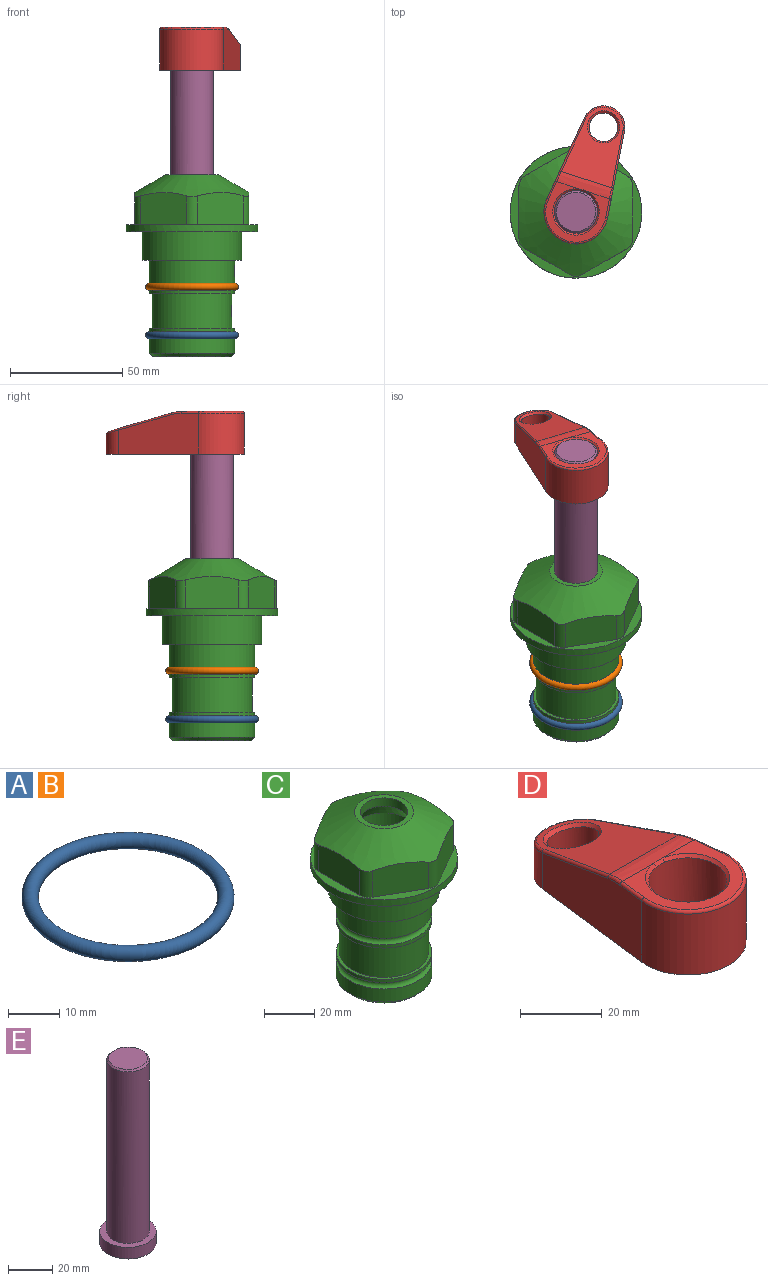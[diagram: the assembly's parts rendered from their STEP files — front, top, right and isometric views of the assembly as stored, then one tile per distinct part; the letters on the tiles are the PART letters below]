
ASSEMBLY  parts=5 mates=4
PART A: 1 faces, bbox 44.7x44.7x3.2 mm
  f0: torus R=19.05mm, axis (0,0,1), area 1193.9mm2
PART B: same geometry as A
PART C: 36 faces, bbox 58.7x58.7x81 mm
  f0: cylinder r=17.78mm len=35.56mm, axis (0,0,1), area 1670.8mm2, adj f23,f24,f31
  f1: cylinder r=19.05mm len=38.1mm, axis (0,0,1), area 1191.9mm2, adj f26,f27,f30
  f2: plane 58.66x58.66mm, normal (0,0,-1), area 1150.6mm2, adj f3,f28
  f3: cylinder r=29.33mm len=58.66mm, axis (0,0,-1), area 585.1mm2, adj f2,f4
  f4: plane 58.66x58.66mm, normal (0,0,1), area 475.9mm2, adj f3,f5,f6,f7,f8,f9,f10,f11
  f5: plane 20.32x14.34mm, normal (-0.5,0.87,0), area 324.4mm2, adj f4,f15,f16,f17
  f6: plane 20.32x14.34mm, normal (0.5,0.87,0), area 324.4mm2, adj f4,f14,f15,f17
  f7: plane 23.48x14.34mm, normal (1,0,0), area 324.4mm2, adj f4,f13,f14,f17
  f8: plane 20.32x14.34mm, normal (0.5,-0.87,0), area 324.4mm2, adj f4,f12,f13,f17
  f9: plane 20.32x14.34mm, normal (-0.5,-0.87,0), area 324.4mm2, adj f4,f11,f12,f17
  f10: plane 23.48x14.34mm, normal (-1,0,0), area 324.4mm2, adj f4,f11,f16,f17
  f11: cylinder r=5.08mm len=12.85mm, axis (0,0,-1), area 67.2mm2, adj f4,f9,f10,f17
  f12: cylinder r=5.08mm len=12.85mm, axis (0,0,-1), area 67.2mm2, adj f4,f8,f9,f17
  f13: cylinder r=5.08mm len=12.85mm, axis (0,0,-1), area 67.2mm2, adj f4,f7,f8,f17
  f14: cylinder r=5.08mm len=12.85mm, axis (0,0,-1), area 67.2mm2, adj f4,f6,f7,f17
  f15: cylinder r=5.08mm len=12.85mm, axis (0,0,-1), area 67.2mm2, adj f4,f5,f6,f17
  f16: cylinder r=5.08mm len=12.85mm, axis (0,0,-1), area 67.2mm2, adj f4,f5,f10,f17
  f17: cone r=11.73mm half-angle=60deg, axis (0,0,-1), area 2071.8mm2, adj f5,f6,f7,f8,f9,f10,f11,f12
  f18: plane 23.46x23.46mm, normal (0,0,1), area 147.4mm2, adj f17,f35
  f19: plane 34.93x34.93mm, normal (0,0,-1), area 958mm2, adj f29
  f20: cylinder r=19.05mm len=38.1mm, axis (0,0,1), area 760.1mm2, adj f21,f29
  f21: torus R=19.05mm, axis (0,0,1), area 565.3mm2, adj f20,f22
  f22: cylinder r=19.05mm len=38.1mm, axis (0,0,1), area 190mm2, adj f21,f23
  f23: plane 38.1x38.1mm, normal (0,0,1), area 146.9mm2, adj f0,f22
  f24: plane 38.1x38.1mm, normal (0,0,-1), area 146.9mm2, adj f0,f25
  f25: cylinder r=19.05mm len=38.1mm, axis (0,0,1), area 190mm2, adj f24,f26
  f26: torus R=19.05mm, axis (0,0,1), area 565.3mm2, adj f1,f25
  f27: plane 44.45x44.45mm, normal (0,0,-1), area 411.7mm2, adj f1,f28
  f28: cylinder r=22.23mm len=44.45mm, axis (0,0,1), area 1773.5mm2, adj f2,f27
  f29: cone r=19.05mm half-angle=45deg, axis (0,0,1), area 257.5mm2, adj f19,f20
  f30: cylinder r=3.17mm len=6.75mm, axis (-1,0,0), area 128mm2, adj f1,f33
  f31: cylinder r=3.17mm len=6.35mm, axis (-1,0,0), area 102.5mm2, adj f0,f33
  f32: plane 25.4x25.4mm, normal (0,0,1), area 506.7mm2, adj f33
  f33: cylinder r=12.7mm len=66.42mm, axis (0,0,-1), area 5236.2mm2, adj f30,f31,f32,f34
  f34: cone r=9.53mm half-angle=30deg, axis (0,0,-1), area 443.4mm2, adj f33,f35
  f35: cylinder r=9.53mm len=19.05mm, axis (0,0,-1), area 240.9mm2, adj f18,f34
PART D: 31 faces, bbox 31.7x65.5x19.8 mm
  f0: plane 39.12x18.26mm, normal (0.99,0.12,0), area 612.2mm2, adj f1,f4,f7,f11,f13,f15
  f1: cylinder r=9.53mm len=18.91mm, axis (0,0,-1), area 296.1mm2, adj f0,f2,f7,f17
  f2: plane 39.12x18.26mm, normal (-0.99,0.12,0), area 612.2mm2, adj f1,f4,f7,f12,f14,f16
  f3: cylinder r=6.35mm len=12.7mm, axis (0,0,-1), area 362.4mm2, adj f7,f18
  f4: cylinder r=14.29mm len=28.58mm, axis (0,0,-1), area 882.2mm2, adj f0,f2,f7,f10
  f5: cylinder r=9.53mm len=19.05mm, axis (0,0,-1), area 1092.6mm2, adj f7,f19,f20
  f6: plane 26.99x23.69mm, normal (0,0,1), area 216.2mm2, adj f9,f10,f11,f12,f19
  f7: plane 63.5x28.58mm, normal (0,0,-1), area 661.8mm2, adj f0,f1,f2,f3,f4,f5,f22,f23
  f8: plane 33.52x23.6mm, normal (0,0.26,0.97), area 486mm2, adj f9,f15,f16,f17,f18
  f9: cylinder r=19.05mm len=24.72mm, axis (1,0,0), area 120.4mm2, adj f6,f8,f13,f14,f20
  f10: torus R=13.49mm, axis (0,0,1), area 59mm2, adj f4,f6,f11,f12
  f11: cylinder r=0.79mm len=8.67mm, axis (0.12,-0.99,0), area 10.8mm2, adj f0,f6,f10,f13
  f12: cylinder r=0.79mm len=8.67mm, axis (0.12,0.99,0), area 10.8mm2, adj f2,f6,f10,f14
  f13: bspline ~4.95x1.42mm, area 6.1mm2, adj f0,f9,f11,f15
  f14: bspline ~4.95x1.42mm, area 6.1mm2, adj f2,f9,f12,f16
  f15: cylinder r=0.79mm len=25.95mm, axis (0.12,-0.96,0.26), area 32.9mm2, adj f0,f8,f13,f17
  f16: cylinder r=0.79mm len=25.95mm, axis (0.12,0.96,-0.26), area 32.9mm2, adj f2,f8,f14,f17
  f17: bspline ~18.91x8.38mm, area 30mm2, adj f1,f8,f15,f16
  f18: bspline ~14.29x14.29mm, area 48.3mm2, adj f3,f8
  f19: cone r=9.53mm half-angle=45deg, axis (0,0,1), area 66.5mm2, adj f5,f6,f20
  f20: bspline ~3.22x0.96mm, area 3.5mm2, adj f5,f9,f19
  f21: plane 2.75x2.72mm, normal (0,0,-1), area 2.9mm2, adj f23,f25,f28
  f22: plane 23.05x15.88mm, normal (-0.99,-0.12,0), area 323.6mm2, adj f7,f25,f26,f27,f28,f29
  f23: plane 23.05x15.88mm, normal (0.99,-0.12,0), area 323.6mm2, adj f7,f21,f25,f27,f28,f30
  f24: cylinder r=9.53mm len=10.69mm, axis (0,0,-1), area 114.7mm2, adj f7,f27,f29,f30
  f25: cylinder r=12.7mm len=20.59mm, axis (0,0,-1), area 381.1mm2, adj f7,f21,f22,f23,f26,f28
  f26: plane 2.75x2.72mm, normal (0,0,-1), area 2.9mm2, adj f22,f25,f28
  f27: plane 19.72x18.37mm, normal (0,-0.26,-0.97), area 291.8mm2, adj f22,f23,f24,f28,f29,f30
  f28: cylinder r=15.88mm len=19.92mm, axis (1,0,0), area 54.8mm2, adj f21,f22,f23,f25,f26,f27
  f29: cylinder r=1.59mm len=11mm, axis (0,0,-1), area 34.7mm2, adj f7,f22,f24,f27
  f30: cylinder r=1.59mm len=11mm, axis (0,0,-1), area 34.7mm2, adj f7,f23,f24,f27
PART E: 6 faces, bbox 25.4x25.4x101.6 mm
  f0: plane 17.46x17.46mm, normal (0,0,1), area 239.5mm2, adj f5
  f1: plane 25.4x25.4mm, normal (0,0,-1), area 506.7mm2, adj f2
  f2: cylinder r=12.7mm len=25.4mm, axis (0,0,1), area 506.7mm2, adj f1,f3
  f3: plane 25.4x25.4mm, normal (0,0,1), area 221.7mm2, adj f2,f4
  f4: cylinder r=9.53mm len=94.46mm, axis (0,0,1), area 5653mm2, adj f3,f5
  f5: cone r=8.73mm half-angle=45deg, axis (0,0,-1), area 64.4mm2, adj f0,f4
PLACE A t=(0,0,-21.59)mm
PLACE B at identity
PLACE C at identity fixed
PLACE D rot(axis=(0,0,-1),18deg) t=(0,0,27.55)mm
PLACE E rot(axis=(0,0,-1),18deg) t=(0,0,27.55)mm
MATE fastened D.f4 <-> E.f2  axis (0,0,1) through (0,0,91.05)mm
MATE fastened B.f0 <-> C.f0  axis (0,0,1) through (0,0,-24.51)mm
MATE cylindrical C.f0 <-> E.f2  axis (0,0,1) through (0,0,-50.55)mm
MATE fastened A.f0 <-> C.f0  axis (0,0,1) through (0,0,-46.1)mm
